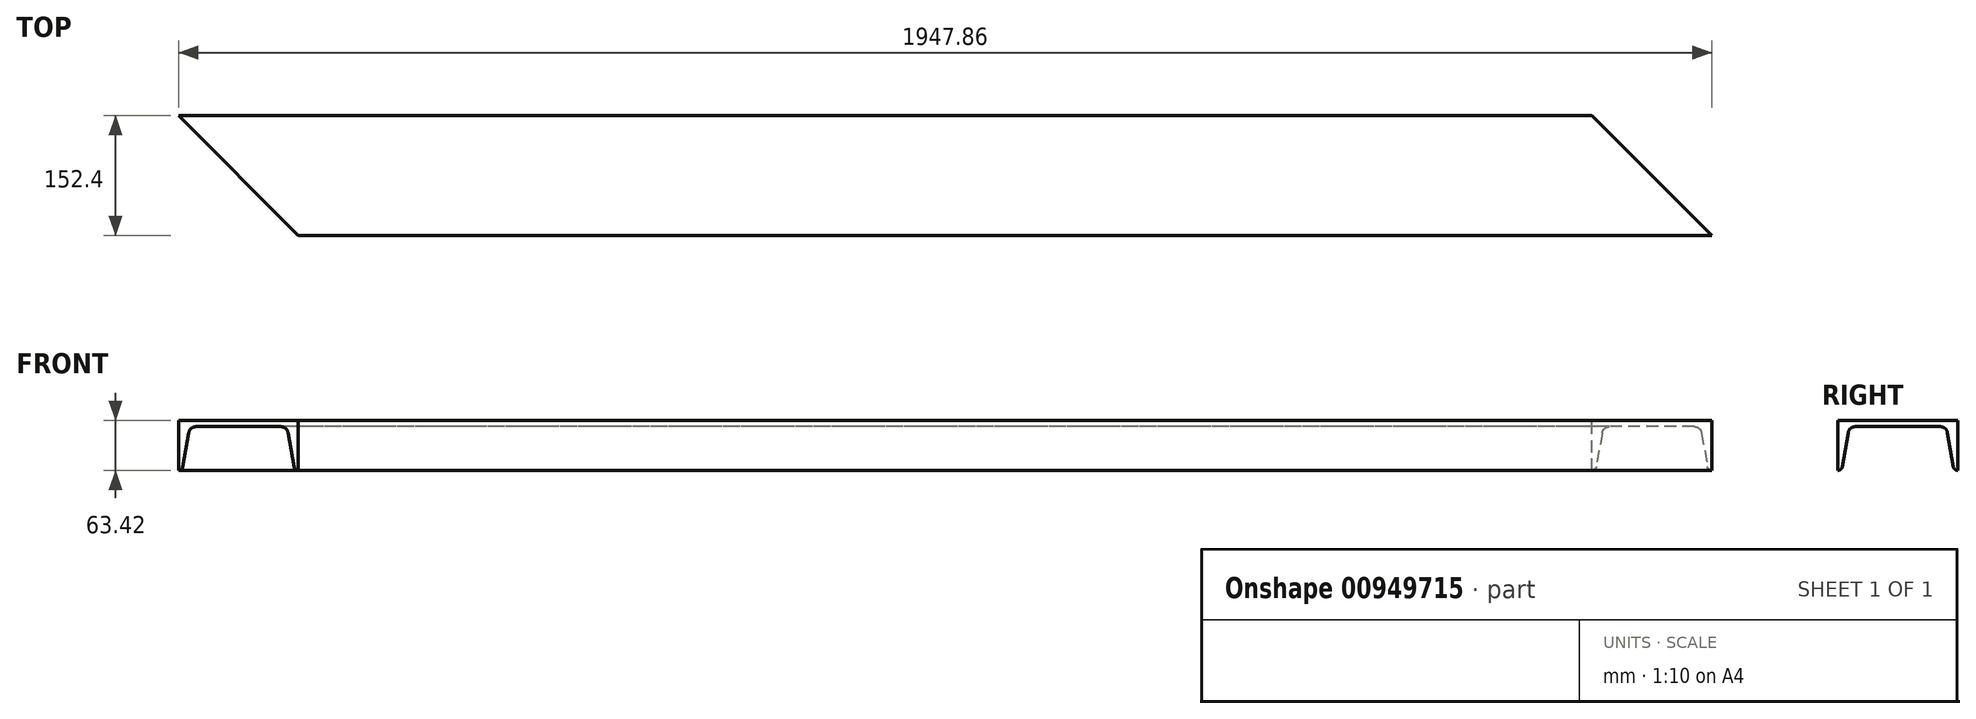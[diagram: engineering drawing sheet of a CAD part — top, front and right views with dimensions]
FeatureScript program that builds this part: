
annotation { "Feature Type Name" : "Feature", "Feature Type Description" : "" }
export const myFeature = defineFeature(function(context is Context, id is Id, definition is map)
    precondition{}
    {
        {
            var Q0;
            Q0=qCreatedBy(makeId("Right.planeOp"),FACE);
            var sketch = newSketch(context, id + "F0", { "sketchPlane" : qUnion([Q0])});
            skLineSegment(sketch, "E0", {"start": v(-76.2, 0) * mm, "end": v(76.2, 0) * mm});
            skLineSegment(sketch, "E1", {"start": v(76.2, 0) * mm, "end": v(76.2, -63.42) * mm});
            skLineSegment(sketch, "E2", {"start": v(-76.2, 0) * mm, "end": v(-76.2, -63.42) * mm});
            skLineSegment(sketch, "E3", {"start": v(-63.12, -15.57) * mm, "end": v(-70.65, -58.76) * mm});
            skLineSegment(sketch, "E4", {"start": v(63.12, -15.57) * mm, "end": v(70.65, -58.76) * mm});
            skLineSegment(sketch, "E5", {"start": v(-53.98, -7.87) * mm, "end": v(53.98, -7.87) * mm});
            skArc(sketch, "E6.filletArc", {"start": v(-76.2, -63.42) * mm, "mid": v(-72.57, -62.1) * mm, "end": v(-70.65, -58.76) * mm});
            skArc(sketch, "E7.filletArc", {"start": v(70.65, -58.76) * mm, "mid": v(72.57, -62.1) * mm, "end": v(76.2, -63.42) * mm});
            skArc(sketch, "E8.filletArc", {"start": v(-53.98, -7.87) * mm, "mid": v(-59.95, -10.05) * mm, "end": v(-63.12, -15.57) * mm});
            skArc(sketch, "E9.filletArc", {"start": v(63.12, -15.57) * mm, "mid": v(59.95, -10.05) * mm, "end": v(53.98, -7.87) * mm});
            skSolve(sketch);
        }
        {
            var Q0;
            Q0=qSketchRegion(id+"F0",true);
            extrude(context, id + "F1", {"entities" : qUnion([Q0]), "depth" : 1947.86 * mm, "offsetDistance" : 25.4 * mm});
        }
        {
            var Q0;
            Q0=makeQuery(id+"F1.opExtrude","SWEPT_FACE",FACE,{"disambiguationData":[OSD([sQuery(id+"F0.wireOp",EDGE,"E0")])]});
            var sketch = newSketch(context, id + "F2", { "sketchPlane" : qUnion([Q0])});
            skLineSegment(sketch, "E10", {"start": v(0, 76.2) * mm, "end": v(152.4, -76.2) * mm});
            skLineSegment(sketch, "E11", {"start": v(152.4, -76.2) * mm, "end": v(0, -76.2) * mm});
            skLineSegment(sketch, "E12", {"start": v(0, -76.2) * mm, "end": v(0, 76.2) * mm});
            skLineSegment(sketch, "E13", {"start": v(1947.86, -76.2) * mm, "end": v(1795.46, 76.2) * mm});
            skLineSegment(sketch, "E14", {"start": v(1795.46, 76.2) * mm, "end": v(1947.86, 76.2) * mm});
            skLineSegment(sketch, "E15", {"start": v(1947.86, 76.2) * mm, "end": v(1947.86, -76.2) * mm});
            skSolve(sketch);
        }
        {
            var Q0;
            Q0 = qSketchRegion(id + "F2", true);
            extrude(context, id + "F3", {"entities" : qUnion([Q0]), "operationType" : NewBodyOperationType.REMOVE, "endBound" : BoundingType.THROUGH_ALL, "oppositeDirection" : true, "depth" : 25.4 * mm, "offsetDistance" : 25.4 * mm});
        }
    });
